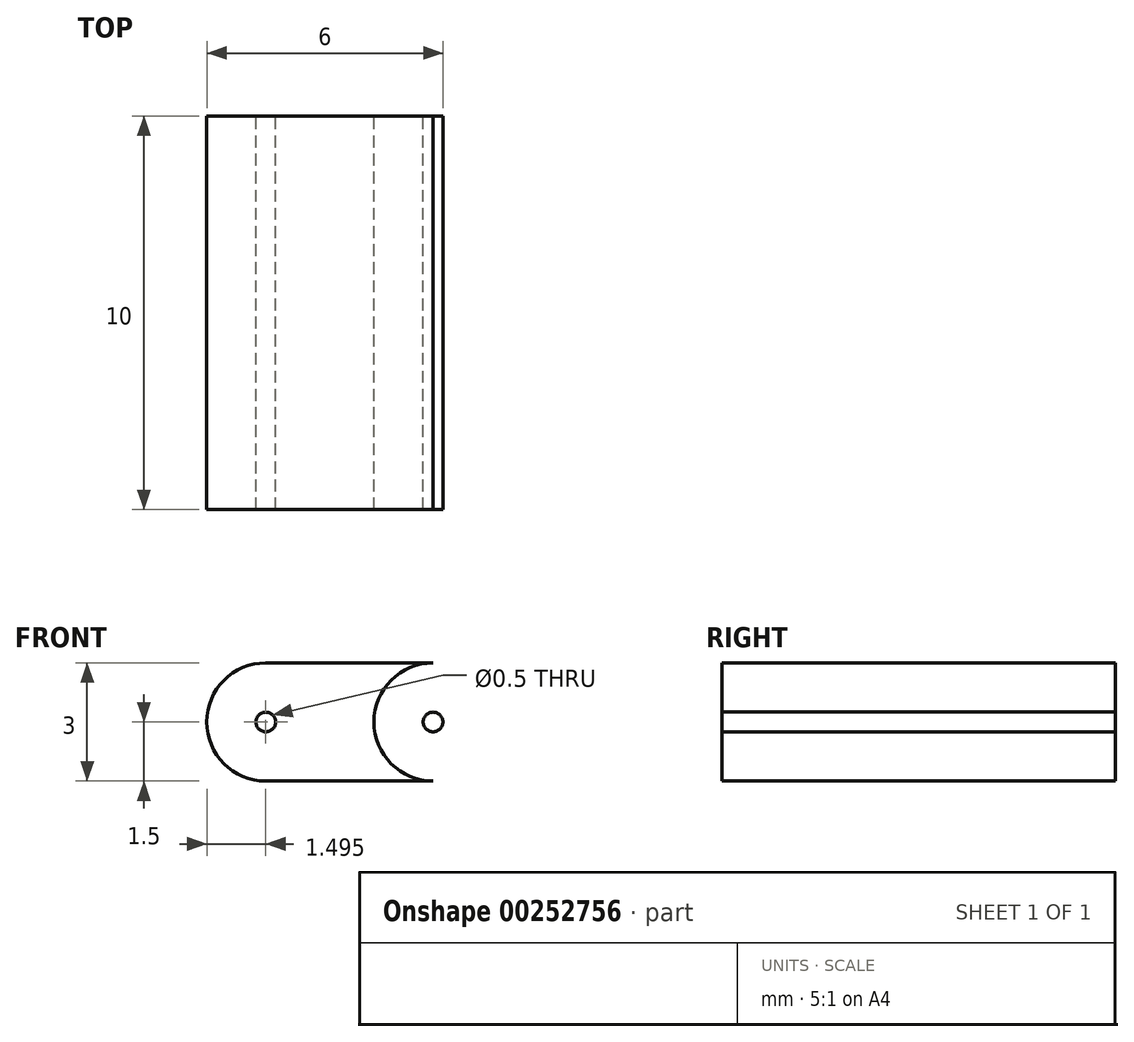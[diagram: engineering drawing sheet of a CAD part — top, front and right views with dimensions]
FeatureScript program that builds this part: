
annotation { "Feature Type Name" : "Feature", "Feature Type Description" : "" }
export const myFeature = defineFeature(function(context is Context, id is Id, definition is map)
    precondition{}
    {
        {
            var Q0;
            Q0=qCreatedBy(makeId("Front.planeOp"),FACE);
            var sketch = newSketch(context, id + "F0", { "sketchPlane" : qUnion([Q0])});
            skLineSegment(sketch, "E0.bottom", {"start": v(-2.13, 1.5) * mm, "end": v(2.13, 1.5) * mm});
            skLineSegment(sketch, "E0.top", {"start": v(-2.12, -1.5) * mm, "end": v(2.13, -1.5) * mm});
            skLineSegment(sketch, "E0.left", {"start": v(-2.12, 1.5) * mm, "end": v(-2.12, -1.5) * mm});
            skLineSegment(sketch, "E0.right", {"start": v(2.13, 1.5) * mm, "end": v(2.13, -1.5) * mm});
            skPoint(sketch, "E0.middle", {"position": v(0, 0) * mm});
            skCircle(sketch, "E1", {"center": v(-2.12, 0) * mm, "radius": 1.5 * mm});
            skCircle(sketch, "E2", {"center": v(2.13, 0) * mm, "radius": 1.5 * mm});
            skCircle(sketch, "E3", {"center": v(-2.12, 0) * mm, "radius": 0.25 * mm});
            skCircle(sketch, "E4.MirrorC", {"center": v(2.12, 0) * mm, "radius": 0.25 * mm});
            skSolve(sketch);
        }
        {
            var Q0;
            {var subQ1=sQuery(id+"F0.wireOp",EDGE,"E0.left");var subQ3=sQuery(id+"F0.wireOp",EDGE,"E3");var subQ4=makeQuery(id+"F0.imprint","INTERSECT",VERTEX,{"disambiguationData":[OD(0.0)],"derivedFrom":[subQ1,subQ3]});Q0=makeQuery(id+"F0.imprint","IMPRINT",FACE,{"disambiguationData":[TD([[makeQuery(id+"F0.imprint","IMPRINT",EDGE,{"disambiguationData":[TD([[subQ4,-1.0]])],"derivedFrom":subQ3}),-1.0]])]});}
            var Q1;
            {var subQ1=sQuery(id+"F0.wireOp",EDGE,"E0.left");var subQ3=sQuery(id+"F0.wireOp",EDGE,"E3");var subQ4=makeQuery(id+"F0.imprint","INTERSECT",VERTEX,{"disambiguationData":[OD(0.0)],"derivedFrom":[subQ1,subQ3]});Q1=makeQuery(id+"F0.imprint","IMPRINT",FACE,{"disambiguationData":[TD([[makeQuery(id+"F0.imprint","IMPRINT",EDGE,{"disambiguationData":[TD([[subQ4,1.0]])],"derivedFrom":subQ3}),-1.0]])]});}
            var Q2;
            {var subQ0=sQuery(id+"F0.wireOp",EDGE,"E0.bottom");Q2=makeQuery(id+"F0.imprint","IMPRINT",FACE,{"disambiguationData":[TD([[makeQuery(id+"F0.imprint","IMPRINT",EDGE,{"derivedFrom":subQ0}),-1.0]])]});}
            var Q3;
            {var subQ1=sQuery(id+"F0.wireOp",EDGE,"E0.right");var subQ3=sQuery(id+"F0.wireOp",EDGE,"E4.MirrorC");var subQ4=makeQuery(id+"F0.imprint","INTERSECT",VERTEX,{"disambiguationData":[OD(0.0)],"derivedFrom":[subQ1,subQ3]});Q3=makeQuery(id+"F0.imprint","IMPRINT",FACE,{"disambiguationData":[TD([[makeQuery(id+"F0.imprint","IMPRINT",EDGE,{"disambiguationData":[TD([[subQ4,1.0]])],"derivedFrom":subQ3}),1.0]])]});}
            var Q4;
            {var subQ1=sQuery(id+"F0.wireOp",EDGE,"E0.right");var subQ3=sQuery(id+"F0.wireOp",EDGE,"E4.MirrorC");var subQ4=makeQuery(id+"F0.imprint","INTERSECT",VERTEX,{"disambiguationData":[OD(0.0)],"derivedFrom":[subQ1,subQ3]});Q4=makeQuery(id+"F0.imprint","IMPRINT",FACE,{"disambiguationData":[TD([[makeQuery(id+"F0.imprint","IMPRINT",EDGE,{"disambiguationData":[TD([[subQ4,-1.0]])],"derivedFrom":subQ3}),1.0]])]});}
            extrude(context, id + "F1", {"entities" : qUnion([Q0, Q1, Q2, Q3, Q4]), "endBound" : BoundingType.SYMMETRIC, "depth" : 10 * mm});
        }
    });
